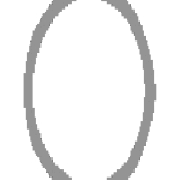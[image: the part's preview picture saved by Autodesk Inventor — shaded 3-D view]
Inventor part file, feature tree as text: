
AUTODESK INVENTOR PART (.ipt)
format: ipt  version: 2021 (Build 250183000, 183)  size: 148,992 bytes
history: native  units: in
note: dims shown in document units (in); Inventor stores cm internally (conversion verified against a paired STEP export)
features: other x5, sketch x2, sweep x1, plane x1
ambient origin geometry x8: Origin, YZ Plane, XZ Plane, XY Plane, X Axis, Y Axis, Z Axis, Center Point
bodies: Solid1 (feature_tree), Body (feature_tree)
feature tree (9):
  other  "Driven Length"
  other  "Frame Generator"
  other  "Start Plane"
  other  "End Plane"
  sweep  "Sweep Path"
  other  "Orientation Work Plane"
  sketch  "Sketch2"  dims[d0=1.0in d1=0.065in]
  plane  "Work Plane3"
  sketch  "Sketch3"  dims[d2=1.1738in d4=-0.0in d5=1.1738in d8=90.0deg d9=1.1738in d10=0.0in d11=0.0in]
